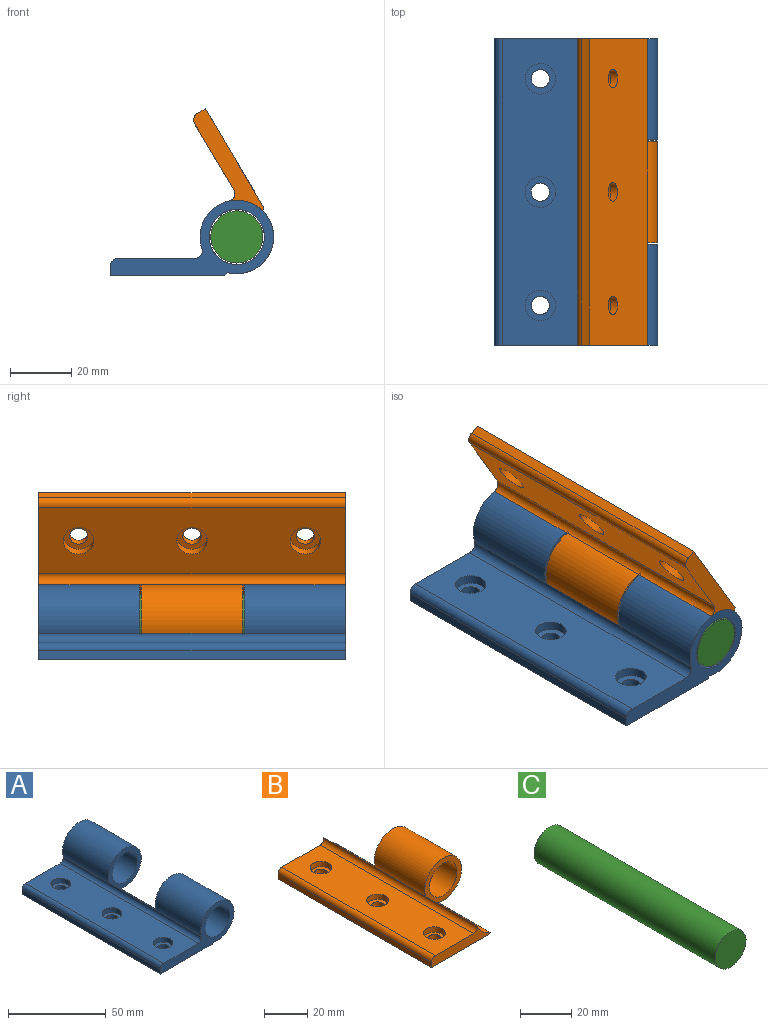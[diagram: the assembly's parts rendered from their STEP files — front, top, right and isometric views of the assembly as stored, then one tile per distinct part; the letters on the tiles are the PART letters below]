
ASSEMBLY  parts=3 mates=2
PART A: 24 faces, bbox 53.3x100x24.5 mm
  f0: cylinder r=12mm len=33mm, axis (0,1,0), area 2103.5mm2, adj f4,f6,f9,f13
  f1: cylinder r=9mm len=33mm, axis (0,-1,0), area 1866.1mm2, adj f9,f13
  f2: plane 100x3mm, normal (-1,0,0), area 300mm2, adj f3,f8,f9,f10
  f3: plane 100x37.37mm, normal (0,0,-1), area 3652.1mm2, adj f2,f4,f8,f9,f21,f22,f23
  f4: plane 100x0.88mm, normal (0.71,0,-0.71), area 124.6mm2, adj f0,f3,f5,f8,f9,f12
  f5: cylinder r=12mm len=33mm, axis (0,1,0), area 2103.5mm2, adj f4,f6,f8,f14
  f6: cylinder r=2.5mm len=100mm, axis (0,1,0), area 435.1mm2, adj f0,f5,f7,f8,f9,f12
  f7: plane 100x25mm, normal (0,0,1), area 2264.4mm2, adj f6,f8,f9,f10,f15,f17,f19
  f8: plane 53.25x24.5mm, normal (0,-1,0), area 390.3mm2, adj f2,f3,f4,f5,f6,f7,f10,f11
  f9: plane 53.25x24.5mm, normal (0,1,0), area 390.3mm2, adj f0,f1,f2,f3,f4,f6,f7,f10
  f10: cylinder r=2.5mm len=100mm, axis (0,1,0), area 392.7mm2, adj f2,f7,f8,f9
  f11: cylinder r=9mm len=33mm, axis (0,-1,0), area 1866.1mm2, adj f8,f14
  f12: cylinder r=12mm len=34mm, axis (0,-1,0), area 396.3mm2, adj f4,f6,f13,f14
  f13: plane 24x24mm, normal (0,-1,0), area 197.9mm2, adj f0,f1,f12
  f14: plane 24x24mm, normal (0,1,0), area 197.9mm2, adj f5,f11,f12
  f15: cylinder r=5mm len=10mm, axis (0,0,1), area 94.2mm2, adj f7,f16
  f16: plane 10x10mm, normal (0,0,1), area 50.3mm2, adj f15,f22
  f17: cylinder r=5mm len=10mm, axis (0,0,1), area 94.2mm2, adj f7,f18
  f18: plane 10x10mm, normal (0,0,1), area 50.3mm2, adj f17,f23
  f19: cylinder r=5mm len=10mm, axis (0,0,1), area 94.2mm2, adj f7,f20
  f20: plane 10x10mm, normal (0,0,1), area 50.3mm2, adj f19,f21
  f21: cylinder r=3mm len=6mm, axis (0,0,-1), area 47.1mm2, adj f3,f20
  f22: cylinder r=3mm len=6mm, axis (0,0,-1), area 47.1mm2, adj f3,f16
  f23: cylinder r=3mm len=6mm, axis (0,0,-1), area 47.1mm2, adj f3,f18
PART B: 23 faces, bbox 53.3x100x24.5 mm
  f0: cylinder r=9mm len=33mm, axis (0,-1,0), area 1866.1mm2, adj f11,f13
  f1: cylinder r=12mm len=33mm, axis (0,1,0), area 2103.5mm2, adj f4,f5,f11,f13
  f2: plane 100x3mm, normal (-1,0,0), area 300mm2, adj f3,f7,f8,f9
  f3: plane 100x37.37mm, normal (0,0,-1), area 3652.1mm2, adj f2,f4,f7,f8,f20,f21,f22
  f4: plane 100x0.88mm, normal (0.71,0,-0.71), area 124.6mm2, adj f1,f3,f7,f8,f10,f12
  f5: cylinder r=2.5mm len=100mm, axis (0,1,0), area 435.1mm2, adj f1,f6,f7,f8,f10,f12
  f6: plane 100x25mm, normal (0,0,1), area 2264.4mm2, adj f5,f7,f8,f9,f14,f16,f18
  f7: plane 38.25x8.42mm, normal (0,-1,0), area 192.4mm2, adj f2,f3,f4,f5,f6,f9,f10
  f8: plane 38.25x8.42mm, normal (0,1,0), area 192.4mm2, adj f2,f3,f4,f5,f6,f9,f12
  f9: cylinder r=2.5mm len=100mm, axis (0,1,0), area 392.7mm2, adj f2,f6,f7,f8
  f10: cylinder r=12mm len=33.5mm, axis (0,-1,0), area 390.5mm2, adj f4,f5,f7,f11
  f11: plane 24x24mm, normal (0,-1,0), area 197.9mm2, adj f0,f1,f10
  f12: cylinder r=12mm len=33.5mm, axis (0,1,0), area 390.5mm2, adj f4,f5,f8,f13
  f13: plane 24x24mm, normal (0,1,0), area 197.9mm2, adj f0,f1,f12
  f14: cylinder r=5mm len=10mm, axis (0,0,1), area 94.2mm2, adj f6,f15
  f15: plane 10x10mm, normal (0,0,1), area 50.3mm2, adj f14,f21
  f16: cylinder r=5mm len=10mm, axis (0,0,1), area 94.2mm2, adj f6,f17
  f17: plane 10x10mm, normal (0,0,1), area 50.3mm2, adj f16,f22
  f18: cylinder r=5mm len=10mm, axis (0,0,1), area 94.2mm2, adj f6,f19
  f19: plane 10x10mm, normal (0,0,1), area 50.3mm2, adj f18,f20
  f20: cylinder r=3mm len=6mm, axis (0,0,-1), area 47.1mm2, adj f3,f19
  f21: cylinder r=3mm len=6mm, axis (0,0,-1), area 47.1mm2, adj f3,f15
  f22: cylinder r=3mm len=6mm, axis (0,0,-1), area 47.1mm2, adj f3,f17
PART C: 3 faces, bbox 17x100x17 mm
  f0: cylinder r=8.5mm len=100mm, axis (0,1,0), area 5340.7mm2, adj f1,f2
  f1: plane 17x17mm, normal (0,-1,0), area 227mm2, adj f0
  f2: plane 17x17mm, normal (0,1,0), area 227mm2, adj f0
PLACE A rot(axis=(0,1,0),0deg) t=(-35.65,2.18,-14.08)mm
PLACE B rot(axis=(-0.87,0,0.5),180deg) t=(-4.67,2.18,40.28)mm
PLACE C t=(5.6,2.18,-1.58)mm fixed
MATE revolute A.f0 <-> C.f0  axis (0,1,0) through (5.6,52.18,-1.58)mm
MATE revolute B.f0 <-> C.f0  axis (0,-1,0) through (5.6,2.18,-1.58)mm
